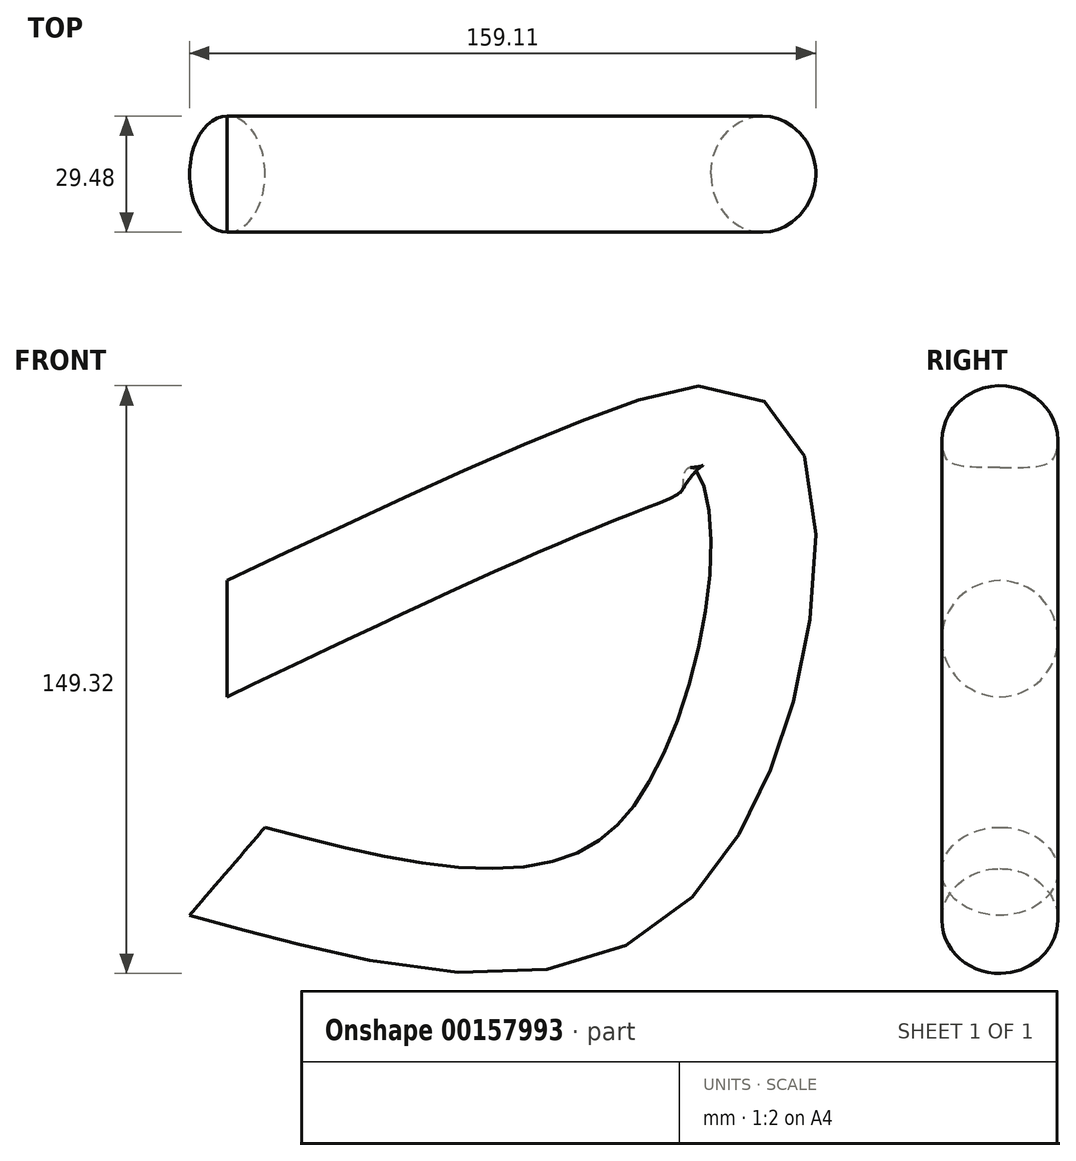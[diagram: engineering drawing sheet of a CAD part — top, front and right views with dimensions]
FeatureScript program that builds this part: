
annotation { "Feature Type Name" : "Feature", "Feature Type Description" : "" }
export const myFeature = defineFeature(function(context is Context, id is Id, definition is map)
    precondition{}
    {
        {
            var Q0;
            Q0=qCreatedBy(makeId("Right.planeOp"),FACE);
            var sketch = newSketch(context, id + "F0", { "sketchPlane" : qUnion([Q0])});
            skCircle(sketch, "E0", {"center": v(0, 0) * mm, "radius": 14.74 * mm});
            skSolve(sketch);
        }
        {
            var Q0;
            Q0=qCreatedBy(makeId("Front.planeOp"),FACE);
            var sketch = newSketch(context, id + "F1", { "sketchPlane" : qUnion([Q0])});
            skFitSpline(sketch, "E1", {"points": [v(0, 0) * mm, v(104.13, 46.33) * mm, v(132.29, 44.37) * mm, v(108.06, -56.48) * mm, v(0, -59.1) * mm], "startDerivative": vector(399.4, 190.03) * mm, "endDerivative": vector(-437.21, 117.9) * mm});
            skSolve(sketch);
        }
        {
            var Q0;
            Q0=makeQuery(id+"F0.imprint","IMPRINT",FACE,{"disambiguationData":[TD([[makeQuery(id+"F0.imprint","IMPRINT",EDGE,{"derivedFrom":sQuery(id+"F0.wireOp",EDGE,"E0")}),1.0]])]});
            var Q1;
            Q1=sQuery(id+"F1.wireOp",EDGE,"E1");
            sweep(context, id + "F2", {"profiles" : qUnion([Q0]), "path" : qUnion([Q1])});
        }
    });
